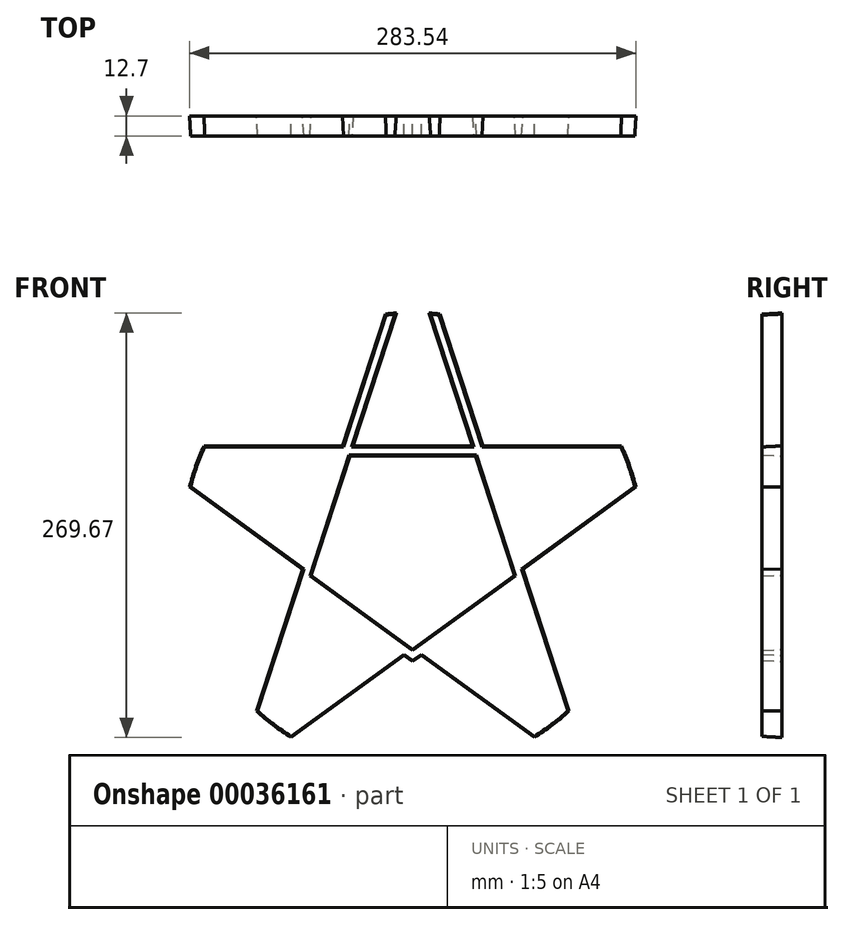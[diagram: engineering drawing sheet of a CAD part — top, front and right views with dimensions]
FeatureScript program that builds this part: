
annotation { "Feature Type Name" : "Feature", "Feature Type Description" : "" }
export const myFeature = defineFeature(function(context is Context, id is Id, definition is map)
    precondition{}
    {
        {
            var Q0;
            Q0=qCreatedBy(makeId("Front.planeOp"),FACE);
            var sketch = newSketch(context, id + "F0", { "sketchPlane" : qUnion([Q0])});
            skCircle(sketch, "E0", {"center": v(0, 0) * mm, "radius": 146.05 * mm});
            skLineSegment(sketch, "E1", {"start": v(-10.44, 145.68) * mm, "end": v(-94.07, -111.72) * mm});
            skLineSegment(sketch, "E2", {"start": v(94.07, -111.72) * mm, "end": v(10.44, 145.68) * mm});
            skCircle(sketch, "E3", {"center": v(0, 0) * mm, "radius": 50 * mm, "construction": true});
            skCircle(sketch, "E4", {"center": v(0, 50) * mm, "radius": 6.5 * mm, "construction": true});
            skCircle(sketch, "E5", {"center": v(0, 50) * mm, "radius": 12.7 * mm, "construction": true});
            skPoint(sketch, "E6.orphan", {"position": v(0, 177.8) * mm});
            skLineSegment(sketch, "E7", {"start": v(99.26, -107.14) * mm, "end": v(17.33, 145.02) * mm});
            skLineSegment(sketch, "E8", {"start": v(-17.33, 145.02) * mm, "end": v(-99.26, -107.14) * mm});
            skCircle(sketch, "E9", {"center": v(0, 0) * mm, "radius": 69.05 * mm, "construction": true});
            skLineSegment(sketch, "E10.1.0", {"start": v(-141.77, 35.09) * mm, "end": v(77.18, -123.99) * mm});
            skLineSegment(sketch, "E10.1.1", {"start": v(-143.28, 28.33) * mm, "end": v(71.22, -127.5) * mm});
            skLineSegment(sketch, "E10.1.2", {"start": v(135.32, 54.94) * mm, "end": v(-135.32, 54.94) * mm});
            skLineSegment(sketch, "E10.1.3", {"start": v(132.57, 61.3) * mm, "end": v(-132.57, 61.3) * mm});
            skLineSegment(sketch, "E10.4.2", {"start": v(-77.18, -123.99) * mm, "end": v(141.77, 35.09) * mm});
            skLineSegment(sketch, "E10.4.3", {"start": v(-71.22, -127.5) * mm, "end": v(143.28, 28.33) * mm});
            skSolve(sketch);
        }
        {
            var Q0;
            {var subQ3=sQuery(id+"F0.wireOp",EDGE,"E1");var subQ5=sQuery(id+"F0.wireOp",EDGE,"E0");var subQ7=makeQuery(id+"F0.imprint","INTERSECT",VERTEX,{"disambiguationData":[OD(0.0)],"derivedFrom":[subQ5,subQ3]});Q0=makeQuery(id+"F0.imprint","IMPRINT",FACE,{"disambiguationData":[TD([[makeQuery(id+"F0.imprint","IMPRINT",EDGE,{"disambiguationData":[TD([[subQ7,-1.0]])],"derivedFrom":subQ5}),1.0]])]});}
            var Q1;
            {var subQ0=sQuery(id+"F0.wireOp",EDGE,"E10.1.3");var subQ3=sQuery(id+"F0.wireOp",EDGE,"E1");var subQ4=makeQuery(id+"F0.imprint","INTERSECT",VERTEX,{"derivedFrom":[subQ3,subQ0]});Q1=makeQuery(id+"F0.imprint","IMPRINT",FACE,{"disambiguationData":[TD([[makeQuery(id+"F0.imprint","IMPRINT",EDGE,{"disambiguationData":[TD([[subQ4,-1.0]])],"derivedFrom":subQ3}),-1.0]])]});}
            var Q2;
            {var subQ0=sQuery(id+"F0.wireOp",EDGE,"E10.1.2");var subQ3=sQuery(id+"F0.wireOp",EDGE,"E1");var subQ4=makeQuery(id+"F0.imprint","INTERSECT",VERTEX,{"derivedFrom":[subQ3,subQ0]});Q2=makeQuery(id+"F0.imprint","IMPRINT",FACE,{"disambiguationData":[TD([[makeQuery(id+"F0.imprint","IMPRINT",EDGE,{"disambiguationData":[TD([[subQ4,-1.0]])],"derivedFrom":subQ3}),-1.0]])]});}
            var Q3;
            {var subQ3=sQuery(id+"F0.wireOp",EDGE,"E0");var subQ5=sQuery(id+"F0.wireOp",EDGE,"E10.1.2");var subQ7=makeQuery(id+"F0.imprint","INTERSECT",VERTEX,{"disambiguationData":[OD(1.0)],"derivedFrom":[subQ3,subQ5]});Q3=makeQuery(id+"F0.imprint","IMPRINT",FACE,{"disambiguationData":[TD([[makeQuery(id+"F0.imprint","IMPRINT",EDGE,{"disambiguationData":[TD([[subQ7,1.0]])],"derivedFrom":subQ3}),1.0]])]});}
            var Q4;
            {var subQ0=sQuery(id+"F0.wireOp",EDGE,"E10.1.3");var subQ3=sQuery(id+"F0.wireOp",EDGE,"E1");var subQ4=makeQuery(id+"F0.imprint","INTERSECT",VERTEX,{"derivedFrom":[subQ3,subQ0]});Q4=makeQuery(id+"F0.imprint","IMPRINT",FACE,{"disambiguationData":[TD([[makeQuery(id+"F0.imprint","IMPRINT",EDGE,{"disambiguationData":[TD([[subQ4,-1.0]])],"derivedFrom":subQ3}),1.0]])]});}
            var Q5;
            {var subQ3=sQuery(id+"F0.wireOp",EDGE,"E0");var subQ5=sQuery(id+"F0.wireOp",EDGE,"E10.1.0");var subQ7=makeQuery(id+"F0.imprint","INTERSECT",VERTEX,{"disambiguationData":[OD(0.0)],"derivedFrom":[subQ3,subQ5]});Q5=makeQuery(id+"F0.imprint","IMPRINT",FACE,{"disambiguationData":[TD([[makeQuery(id+"F0.imprint","IMPRINT",EDGE,{"disambiguationData":[TD([[subQ7,-1.0]])],"derivedFrom":subQ3}),1.0]])]});}
            var Q6;
            {var subQ3=sQuery(id+"F0.wireOp",EDGE,"E1");var subQ5=sQuery(id+"F0.wireOp",EDGE,"E10.1.0");var subQ7=makeQuery(id+"F0.imprint","INTERSECT",VERTEX,{"derivedFrom":[subQ3,subQ5]});Q6=makeQuery(id+"F0.imprint","IMPRINT",FACE,{"disambiguationData":[TD([[makeQuery(id+"F0.imprint","IMPRINT",EDGE,{"disambiguationData":[TD([[subQ7,-1.0]])],"derivedFrom":subQ3}),-1.0]])]});}
            var Q7;
            {var subQ3=sQuery(id+"F0.wireOp",EDGE,"E10.1.0");var subQ5=sQuery(id+"F0.wireOp",EDGE,"E1");var subQ7=makeQuery(id+"F0.imprint","INTERSECT",VERTEX,{"derivedFrom":[subQ5,subQ3]});Q7=makeQuery(id+"F0.imprint","IMPRINT",FACE,{"disambiguationData":[TD([[makeQuery(id+"F0.imprint","IMPRINT",EDGE,{"disambiguationData":[TD([[subQ7,-1.0]])],"derivedFrom":subQ5}),1.0]])]});}
            var Q8;
            {var subQ3=sQuery(id+"F0.wireOp",EDGE,"E1");var subQ5=sQuery(id+"F0.wireOp",EDGE,"E0");var subQ7=makeQuery(id+"F0.imprint","INTERSECT",VERTEX,{"disambiguationData":[OD(1.0)],"derivedFrom":[subQ5,subQ3]});Q8=makeQuery(id+"F0.imprint","IMPRINT",FACE,{"disambiguationData":[TD([[makeQuery(id+"F0.imprint","IMPRINT",EDGE,{"disambiguationData":[TD([[subQ7,1.0]])],"derivedFrom":subQ5}),1.0]])]});}
            var Q9;
            {var subQ3=sQuery(id+"F0.wireOp",EDGE,"E0");var subQ5=sQuery(id+"F0.wireOp",EDGE,"E10.4.2");var subQ7=makeQuery(id+"F0.imprint","INTERSECT",VERTEX,{"disambiguationData":[OD(0.0)],"derivedFrom":[subQ3,subQ5]});Q9=makeQuery(id+"F0.imprint","IMPRINT",FACE,{"disambiguationData":[TD([[makeQuery(id+"F0.imprint","IMPRINT",EDGE,{"disambiguationData":[TD([[subQ7,-1.0]])],"derivedFrom":subQ3}),1.0]])]});}
            var Q10;
            {var subQ3=sQuery(id+"F0.wireOp",EDGE,"E10.1.0");var subQ5=sQuery(id+"F0.wireOp",EDGE,"E0");var subQ7=makeQuery(id+"F0.imprint","INTERSECT",VERTEX,{"disambiguationData":[OD(1.0)],"derivedFrom":[subQ5,subQ3]});Q10=makeQuery(id+"F0.imprint","IMPRINT",FACE,{"disambiguationData":[TD([[makeQuery(id+"F0.imprint","IMPRINT",EDGE,{"disambiguationData":[TD([[subQ7,1.0]])],"derivedFrom":subQ5}),1.0]])]});}
            var Q11;
            {var subQ0=sQuery(id+"F0.wireOp",EDGE,"E10.4.3");var subQ3=sQuery(id+"F0.wireOp",EDGE,"E2");var subQ4=makeQuery(id+"F0.imprint","INTERSECT",VERTEX,{"derivedFrom":[subQ3,subQ0]});Q11=makeQuery(id+"F0.imprint","IMPRINT",FACE,{"disambiguationData":[TD([[makeQuery(id+"F0.imprint","IMPRINT",EDGE,{"disambiguationData":[TD([[subQ4,-1.0]])],"derivedFrom":subQ3}),1.0]])]});}
            var Q12;
            {var subQ3=sQuery(id+"F0.wireOp",EDGE,"E10.1.0");var subQ5=sQuery(id+"F0.wireOp",EDGE,"E10.4.2");var subQ7=makeQuery(id+"F0.imprint","INTERSECT",VERTEX,{"derivedFrom":[subQ3,subQ5]});Q12=makeQuery(id+"F0.imprint","IMPRINT",FACE,{"disambiguationData":[TD([[makeQuery(id+"F0.imprint","IMPRINT",EDGE,{"disambiguationData":[TD([[subQ7,-1.0]])],"derivedFrom":subQ3}),-1.0]])]});}
            var Q13;
            {var subQ0=sQuery(id+"F0.wireOp",EDGE,"E10.4.3");var subQ3=sQuery(id+"F0.wireOp",EDGE,"E2");var subQ4=makeQuery(id+"F0.imprint","INTERSECT",VERTEX,{"derivedFrom":[subQ3,subQ0]});Q13=makeQuery(id+"F0.imprint","IMPRINT",FACE,{"disambiguationData":[TD([[makeQuery(id+"F0.imprint","IMPRINT",EDGE,{"disambiguationData":[TD([[subQ4,-1.0]])],"derivedFrom":subQ3}),-1.0]])]});}
            var Q14;
            {var subQ3=sQuery(id+"F0.wireOp",EDGE,"E0");var subQ5=sQuery(id+"F0.wireOp",EDGE,"E2");var subQ7=makeQuery(id+"F0.imprint","INTERSECT",VERTEX,{"disambiguationData":[OD(0.0)],"derivedFrom":[subQ3,subQ5]});Q14=makeQuery(id+"F0.imprint","IMPRINT",FACE,{"disambiguationData":[TD([[makeQuery(id+"F0.imprint","IMPRINT",EDGE,{"disambiguationData":[TD([[subQ7,-1.0]])],"derivedFrom":subQ3}),1.0]])]});}
            var Q15;
            {var subQ0=sQuery(id+"F0.wireOp",EDGE,"E10.4.2");var subQ3=sQuery(id+"F0.wireOp",EDGE,"E0");var subQ4=makeQuery(id+"F0.imprint","INTERSECT",VERTEX,{"disambiguationData":[OD(1.0)],"derivedFrom":[subQ3,subQ0]});Q15=makeQuery(id+"F0.imprint","IMPRINT",FACE,{"disambiguationData":[TD([[makeQuery(id+"F0.imprint","IMPRINT",EDGE,{"disambiguationData":[TD([[subQ4,1.0]])],"derivedFrom":subQ3}),1.0]])]});}
            var Q16;
            {var subQ0=sQuery(id+"F0.wireOp",EDGE,"E10.4.2");var subQ3=sQuery(id+"F0.wireOp",EDGE,"E2");var subQ4=makeQuery(id+"F0.imprint","INTERSECT",VERTEX,{"derivedFrom":[subQ3,subQ0]});Q16=makeQuery(id+"F0.imprint","IMPRINT",FACE,{"disambiguationData":[TD([[makeQuery(id+"F0.imprint","IMPRINT",EDGE,{"disambiguationData":[TD([[subQ4,-1.0]])],"derivedFrom":subQ3}),-1.0]])]});}
            var Q17;
            {var subQ0=sQuery(id+"F0.wireOp",EDGE,"E10.1.2");var subQ3=sQuery(id+"F0.wireOp",EDGE,"E0");var subQ4=makeQuery(id+"F0.imprint","INTERSECT",VERTEX,{"disambiguationData":[OD(0.0)],"derivedFrom":[subQ3,subQ0]});Q17=makeQuery(id+"F0.imprint","IMPRINT",FACE,{"disambiguationData":[TD([[makeQuery(id+"F0.imprint","IMPRINT",EDGE,{"disambiguationData":[TD([[subQ4,-1.0]])],"derivedFrom":subQ3}),1.0]])]});}
            var Q18;
            {var subQ3=sQuery(id+"F0.wireOp",EDGE,"E2");var subQ5=sQuery(id+"F0.wireOp",EDGE,"E0");var subQ6=makeQuery(id+"F0.imprint","INTERSECT",VERTEX,{"disambiguationData":[OD(1.0)],"derivedFrom":[subQ5,subQ3]});Q18=makeQuery(id+"F0.imprint","IMPRINT",FACE,{"disambiguationData":[TD([[makeQuery(id+"F0.imprint","IMPRINT",EDGE,{"disambiguationData":[TD([[subQ6,1.0]])],"derivedFrom":subQ5}),1.0]])]});}
            var Q19;
            {var subQ3=sQuery(id+"F0.wireOp",EDGE,"E2");var subQ5=sQuery(id+"F0.wireOp",EDGE,"E10.1.2");var subQ7=makeQuery(id+"F0.imprint","INTERSECT",VERTEX,{"derivedFrom":[subQ3,subQ5]});Q19=makeQuery(id+"F0.imprint","IMPRINT",FACE,{"disambiguationData":[TD([[makeQuery(id+"F0.imprint","IMPRINT",EDGE,{"disambiguationData":[TD([[subQ7,-1.0]])],"derivedFrom":subQ3}),-1.0]])]});}
            extrude(context, id + "F1", {"entities" : qUnion([Q0, Q1, Q2, Q3, Q4, Q5, Q6, Q7, Q8, Q9, Q10, Q11, Q12, Q13, Q14, Q15, Q16, Q17, Q18, Q19]), "depth" : 12.7 * mm, "hasDraft" : true, "draftAngle" : 3 * degree, "draftPullDirection" : true});
        }
    });
